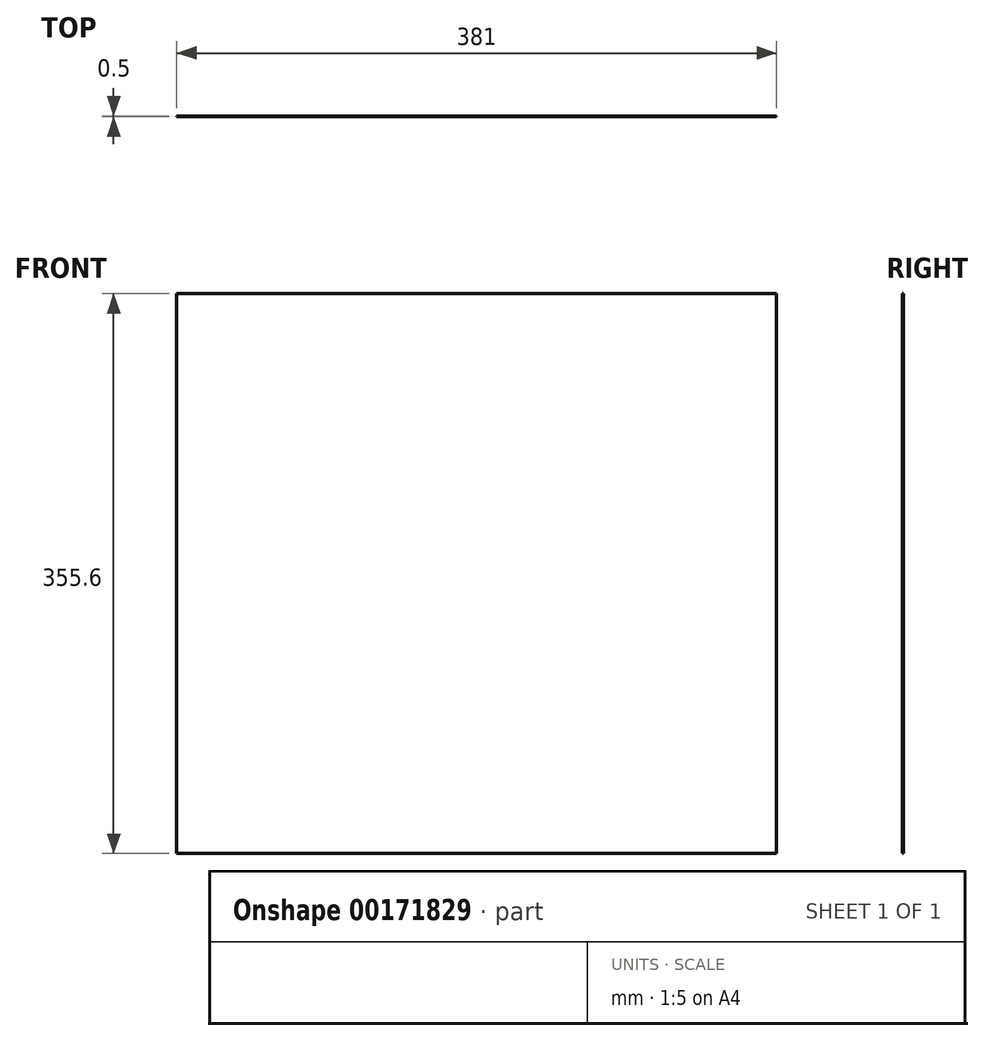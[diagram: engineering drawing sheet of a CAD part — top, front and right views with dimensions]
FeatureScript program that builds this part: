
annotation { "Feature Type Name" : "Feature", "Feature Type Description" : "" }
export const myFeature = defineFeature(function(context is Context, id is Id, definition is map)
    precondition{}
    {
        {
            var Q0;
            Q0=qCreatedBy(makeId("Front.planeOp"),FACE);
            var sketch = newSketch(context, id + "F0", { "sketchPlane" : qUnion([Q0])});
            skLineSegment(sketch, "E0.bottom", {"start": v(0, 0) * mm, "end": v(381, 0) * mm});
            skLineSegment(sketch, "E0.top", {"start": v(0, -355.6) * mm, "end": v(381, -355.6) * mm});
            skLineSegment(sketch, "E0.left", {"start": v(0, 0) * mm, "end": v(0, -355.6) * mm});
            skLineSegment(sketch, "E0.right", {"start": v(381, 0) * mm, "end": v(381, -355.6) * mm});
            skSolve(sketch);
        }
        {
            assignVariable(context, id + "F1", {"name" : "board_thickness", "anyValue" : .5});
        }
        {
            var Q0;
            Q0=makeQuery(id+"F0.imprint","IMPRINT",FACE,{"disambiguationData":[TD([[makeQuery(id+"F0.imprint","IMPRINT",EDGE,{"derivedFrom":sQuery(id+"F0.wireOp",EDGE,"E0.bottom")}),-1.0]])]});
            extrude(context, id + "F2", {"entities" : qUnion([Q0]), "depth" : (getVariable(context, 'board_thickness')) * mm});
        }
    });
